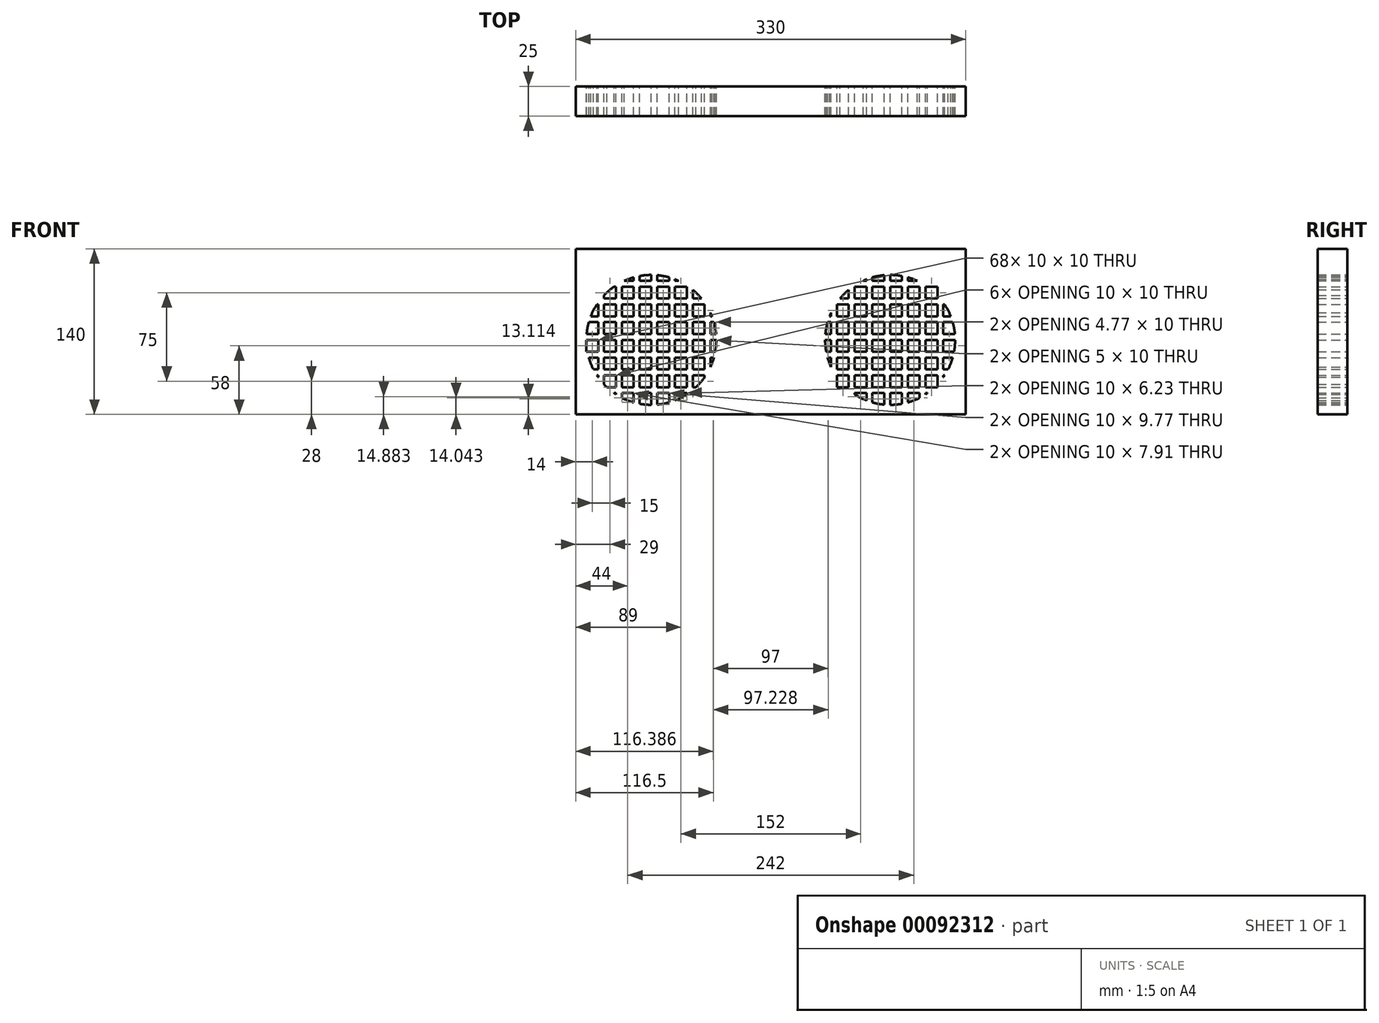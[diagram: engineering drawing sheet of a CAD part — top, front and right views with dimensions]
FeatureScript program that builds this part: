
annotation { "Feature Type Name" : "Feature", "Feature Type Description" : "" }
export const myFeature = defineFeature(function(context is Context, id is Id, definition is map)
    precondition{}
    {
        {
            var Q0;
            Q0=qCreatedBy(makeId("Front.planeOp"),FACE);
            var sketch = newSketch(context, id + "F0", { "sketchPlane" : qUnion([Q0])});
            skLineSegment(sketch, "E0.bottom", {"start": v(0, 0) * mm, "end": v(-165, 0) * mm});
            skLineSegment(sketch, "E0.top", {"start": v(0, 140) * mm, "end": v(-165, 140) * mm});
            skLineSegment(sketch, "E0.left", {"start": v(0, 0) * mm, "end": v(0, 140) * mm});
            skLineSegment(sketch, "E0.right", {"start": v(-165, 0) * mm, "end": v(-165, 140) * mm});
            skCircle(sketch, "E1", {"center": v(-101, 63) * mm, "radius": 55 * mm});
            skLineSegment(sketch, "E2.bottom", {"start": v(-156, 8) * mm, "end": v(-146, 8) * mm});
            skLineSegment(sketch, "E2.top", {"start": v(-156, 18) * mm, "end": v(-146, 18) * mm});
            skLineSegment(sketch, "E2.left", {"start": v(-156, 8) * mm, "end": v(-156, 18) * mm});
            skLineSegment(sketch, "E2.right", {"start": v(-146, 8) * mm, "end": v(-146, 18) * mm});
            skLineSegment(sketch, "E3.0.1.0", {"start": v(-156, 23) * mm, "end": v(-146, 23) * mm});
            skLineSegment(sketch, "E3.0.1.1", {"start": v(-156, 33) * mm, "end": v(-146, 33) * mm});
            skLineSegment(sketch, "E3.0.1.2", {"start": v(-156, 23) * mm, "end": v(-156, 33) * mm});
            skLineSegment(sketch, "E3.0.1.3", {"start": v(-146, 23) * mm, "end": v(-146, 33) * mm});
            skLineSegment(sketch, "E3.0.2.0", {"start": v(-156, 38) * mm, "end": v(-146, 38) * mm});
            skLineSegment(sketch, "E3.0.2.1", {"start": v(-156, 48) * mm, "end": v(-146, 48) * mm});
            skLineSegment(sketch, "E3.0.2.2", {"start": v(-156, 38) * mm, "end": v(-156, 48) * mm});
            skLineSegment(sketch, "E3.0.2.3", {"start": v(-146, 38) * mm, "end": v(-146, 48) * mm});
            skLineSegment(sketch, "E3.0.3.0", {"start": v(-156, 53) * mm, "end": v(-146, 53) * mm});
            skLineSegment(sketch, "E3.0.3.1", {"start": v(-156, 63) * mm, "end": v(-146, 63) * mm});
            skLineSegment(sketch, "E3.0.3.2", {"start": v(-156, 53) * mm, "end": v(-156, 63) * mm});
            skLineSegment(sketch, "E3.0.3.3", {"start": v(-146, 53) * mm, "end": v(-146, 63) * mm});
            skLineSegment(sketch, "E3.0.4.0", {"start": v(-156, 68) * mm, "end": v(-146, 68) * mm});
            skLineSegment(sketch, "E3.0.4.1", {"start": v(-156, 78) * mm, "end": v(-146, 78) * mm});
            skLineSegment(sketch, "E3.0.4.2", {"start": v(-156, 68) * mm, "end": v(-156, 78) * mm});
            skLineSegment(sketch, "E3.0.4.3", {"start": v(-146, 68) * mm, "end": v(-146, 78) * mm});
            skLineSegment(sketch, "E3.0.5.0", {"start": v(-156, 83) * mm, "end": v(-146, 83) * mm});
            skLineSegment(sketch, "E3.0.5.1", {"start": v(-156, 93) * mm, "end": v(-146, 93) * mm});
            skLineSegment(sketch, "E3.0.5.2", {"start": v(-156, 83) * mm, "end": v(-156, 93) * mm});
            skLineSegment(sketch, "E3.0.5.3", {"start": v(-146, 83) * mm, "end": v(-146, 93) * mm});
            skLineSegment(sketch, "E3.0.6.0", {"start": v(-156, 98) * mm, "end": v(-146, 98) * mm});
            skLineSegment(sketch, "E3.0.6.1", {"start": v(-156, 108) * mm, "end": v(-146, 108) * mm});
            skLineSegment(sketch, "E3.0.6.2", {"start": v(-156, 98) * mm, "end": v(-156, 108) * mm});
            skLineSegment(sketch, "E3.0.6.3", {"start": v(-146, 98) * mm, "end": v(-146, 108) * mm});
            skLineSegment(sketch, "E3.1.0.0", {"start": v(-141, 8) * mm, "end": v(-131, 8) * mm});
            skLineSegment(sketch, "E3.1.0.1", {"start": v(-141, 18) * mm, "end": v(-131, 18) * mm});
            skLineSegment(sketch, "E3.1.0.2", {"start": v(-141, 8) * mm, "end": v(-141, 18) * mm});
            skLineSegment(sketch, "E3.1.0.3", {"start": v(-131, 8) * mm, "end": v(-131, 18) * mm});
            skLineSegment(sketch, "E3.1.1.0", {"start": v(-141, 23) * mm, "end": v(-131, 23) * mm});
            skLineSegment(sketch, "E3.1.1.1", {"start": v(-141, 33) * mm, "end": v(-131, 33) * mm});
            skLineSegment(sketch, "E3.1.1.2", {"start": v(-141, 23) * mm, "end": v(-141, 33) * mm});
            skLineSegment(sketch, "E3.1.1.3", {"start": v(-131, 23) * mm, "end": v(-131, 33) * mm});
            skLineSegment(sketch, "E3.1.2.0", {"start": v(-141, 38) * mm, "end": v(-131, 38) * mm});
            skLineSegment(sketch, "E3.1.2.1", {"start": v(-141, 48) * mm, "end": v(-131, 48) * mm});
            skLineSegment(sketch, "E3.1.2.2", {"start": v(-141, 38) * mm, "end": v(-141, 48) * mm});
            skLineSegment(sketch, "E3.1.2.3", {"start": v(-131, 38) * mm, "end": v(-131, 48) * mm});
            skLineSegment(sketch, "E3.1.3.0", {"start": v(-141, 53) * mm, "end": v(-131, 53) * mm});
            skLineSegment(sketch, "E3.1.3.1", {"start": v(-141, 63) * mm, "end": v(-131, 63) * mm});
            skLineSegment(sketch, "E3.1.3.2", {"start": v(-141, 53) * mm, "end": v(-141, 63) * mm});
            skLineSegment(sketch, "E3.1.3.3", {"start": v(-131, 53) * mm, "end": v(-131, 63) * mm});
            skLineSegment(sketch, "E3.1.4.0", {"start": v(-141, 68) * mm, "end": v(-131, 68) * mm});
            skLineSegment(sketch, "E3.1.4.1", {"start": v(-141, 78) * mm, "end": v(-131, 78) * mm});
            skLineSegment(sketch, "E3.1.4.2", {"start": v(-141, 68) * mm, "end": v(-141, 78) * mm});
            skLineSegment(sketch, "E3.1.4.3", {"start": v(-131, 68) * mm, "end": v(-131, 78) * mm});
            skLineSegment(sketch, "E3.1.5.0", {"start": v(-141, 83) * mm, "end": v(-131, 83) * mm});
            skLineSegment(sketch, "E3.1.5.1", {"start": v(-141, 93) * mm, "end": v(-131, 93) * mm});
            skLineSegment(sketch, "E3.1.5.2", {"start": v(-141, 83) * mm, "end": v(-141, 93) * mm});
            skLineSegment(sketch, "E3.1.5.3", {"start": v(-131, 83) * mm, "end": v(-131, 93) * mm});
            skLineSegment(sketch, "E3.1.6.0", {"start": v(-141, 98) * mm, "end": v(-131, 98) * mm});
            skLineSegment(sketch, "E3.1.6.1", {"start": v(-141, 108) * mm, "end": v(-131, 108) * mm});
            skLineSegment(sketch, "E3.1.6.2", {"start": v(-141, 98) * mm, "end": v(-141, 108) * mm});
            skLineSegment(sketch, "E3.1.6.3", {"start": v(-131, 98) * mm, "end": v(-131, 108) * mm});
            skLineSegment(sketch, "E3.2.0.0", {"start": v(-126, 8) * mm, "end": v(-116, 8) * mm});
            skLineSegment(sketch, "E3.2.0.1", {"start": v(-126, 18) * mm, "end": v(-116, 18) * mm});
            skLineSegment(sketch, "E3.2.0.2", {"start": v(-126, 8) * mm, "end": v(-126, 18) * mm});
            skLineSegment(sketch, "E3.2.0.3", {"start": v(-116, 8) * mm, "end": v(-116, 18) * mm});
            skLineSegment(sketch, "E3.2.1.0", {"start": v(-126, 23) * mm, "end": v(-116, 23) * mm});
            skLineSegment(sketch, "E3.2.1.1", {"start": v(-126, 33) * mm, "end": v(-116, 33) * mm});
            skLineSegment(sketch, "E3.2.1.2", {"start": v(-126, 23) * mm, "end": v(-126, 33) * mm});
            skLineSegment(sketch, "E3.2.1.3", {"start": v(-116, 23) * mm, "end": v(-116, 33) * mm});
            skLineSegment(sketch, "E3.2.2.0", {"start": v(-126, 38) * mm, "end": v(-116, 38) * mm});
            skLineSegment(sketch, "E3.2.2.1", {"start": v(-126, 48) * mm, "end": v(-116, 48) * mm});
            skLineSegment(sketch, "E3.2.2.2", {"start": v(-126, 38) * mm, "end": v(-126, 48) * mm});
            skLineSegment(sketch, "E3.2.2.3", {"start": v(-116, 38) * mm, "end": v(-116, 48) * mm});
            skLineSegment(sketch, "E3.2.3.0", {"start": v(-126, 53) * mm, "end": v(-116, 53) * mm});
            skLineSegment(sketch, "E3.2.3.1", {"start": v(-126, 63) * mm, "end": v(-116, 63) * mm});
            skLineSegment(sketch, "E3.2.3.2", {"start": v(-126, 53) * mm, "end": v(-126, 63) * mm});
            skLineSegment(sketch, "E3.2.3.3", {"start": v(-116, 53) * mm, "end": v(-116, 63) * mm});
            skLineSegment(sketch, "E3.2.4.0", {"start": v(-126, 68) * mm, "end": v(-116, 68) * mm});
            skLineSegment(sketch, "E3.2.4.1", {"start": v(-126, 78) * mm, "end": v(-116, 78) * mm});
            skLineSegment(sketch, "E3.2.4.2", {"start": v(-126, 68) * mm, "end": v(-126, 78) * mm});
            skLineSegment(sketch, "E3.2.4.3", {"start": v(-116, 68) * mm, "end": v(-116, 78) * mm});
            skLineSegment(sketch, "E3.2.5.0", {"start": v(-126, 83) * mm, "end": v(-116, 83) * mm});
            skLineSegment(sketch, "E3.2.5.1", {"start": v(-126, 93) * mm, "end": v(-116, 93) * mm});
            skLineSegment(sketch, "E3.2.5.2", {"start": v(-126, 83) * mm, "end": v(-126, 93) * mm});
            skLineSegment(sketch, "E3.2.5.3", {"start": v(-116, 83) * mm, "end": v(-116, 93) * mm});
            skLineSegment(sketch, "E3.2.6.0", {"start": v(-126, 98) * mm, "end": v(-116, 98) * mm});
            skLineSegment(sketch, "E3.2.6.1", {"start": v(-126, 108) * mm, "end": v(-116, 108) * mm});
            skLineSegment(sketch, "E3.2.6.2", {"start": v(-126, 98) * mm, "end": v(-126, 108) * mm});
            skLineSegment(sketch, "E3.2.6.3", {"start": v(-116, 98) * mm, "end": v(-116, 108) * mm});
            skLineSegment(sketch, "E3.3.0.0", {"start": v(-111, 8) * mm, "end": v(-101, 8) * mm});
            skLineSegment(sketch, "E3.3.0.1", {"start": v(-111, 18) * mm, "end": v(-101, 18) * mm});
            skLineSegment(sketch, "E3.3.0.2", {"start": v(-111, 8) * mm, "end": v(-111, 18) * mm});
            skLineSegment(sketch, "E3.3.0.3", {"start": v(-101, 8) * mm, "end": v(-101, 18) * mm});
            skLineSegment(sketch, "E3.3.1.0", {"start": v(-111, 23) * mm, "end": v(-101, 23) * mm});
            skLineSegment(sketch, "E3.3.1.1", {"start": v(-111, 33) * mm, "end": v(-101, 33) * mm});
            skLineSegment(sketch, "E3.3.1.2", {"start": v(-111, 23) * mm, "end": v(-111, 33) * mm});
            skLineSegment(sketch, "E3.3.1.3", {"start": v(-101, 23) * mm, "end": v(-101, 33) * mm});
            skLineSegment(sketch, "E3.3.2.0", {"start": v(-111, 38) * mm, "end": v(-101, 38) * mm});
            skLineSegment(sketch, "E3.3.2.1", {"start": v(-111, 48) * mm, "end": v(-101, 48) * mm});
            skLineSegment(sketch, "E3.3.2.2", {"start": v(-111, 38) * mm, "end": v(-111, 48) * mm});
            skLineSegment(sketch, "E3.3.2.3", {"start": v(-101, 38) * mm, "end": v(-101, 48) * mm});
            skLineSegment(sketch, "E3.3.3.0", {"start": v(-111, 53) * mm, "end": v(-101, 53) * mm});
            skLineSegment(sketch, "E3.3.3.1", {"start": v(-111, 63) * mm, "end": v(-101, 63) * mm});
            skLineSegment(sketch, "E3.3.3.2", {"start": v(-111, 53) * mm, "end": v(-111, 63) * mm});
            skLineSegment(sketch, "E3.3.3.3", {"start": v(-101, 53) * mm, "end": v(-101, 63) * mm});
            skLineSegment(sketch, "E3.3.4.0", {"start": v(-111, 68) * mm, "end": v(-101, 68) * mm});
            skLineSegment(sketch, "E3.3.4.1", {"start": v(-111, 78) * mm, "end": v(-101, 78) * mm});
            skLineSegment(sketch, "E3.3.4.2", {"start": v(-111, 68) * mm, "end": v(-111, 78) * mm});
            skLineSegment(sketch, "E3.3.4.3", {"start": v(-101, 68) * mm, "end": v(-101, 78) * mm});
            skLineSegment(sketch, "E3.3.5.0", {"start": v(-111, 83) * mm, "end": v(-101, 83) * mm});
            skLineSegment(sketch, "E3.3.5.1", {"start": v(-111, 93) * mm, "end": v(-101, 93) * mm});
            skLineSegment(sketch, "E3.3.5.2", {"start": v(-111, 83) * mm, "end": v(-111, 93) * mm});
            skLineSegment(sketch, "E3.3.5.3", {"start": v(-101, 83) * mm, "end": v(-101, 93) * mm});
            skLineSegment(sketch, "E3.3.6.0", {"start": v(-111, 98) * mm, "end": v(-101, 98) * mm});
            skLineSegment(sketch, "E3.3.6.1", {"start": v(-111, 108) * mm, "end": v(-101, 108) * mm});
            skLineSegment(sketch, "E3.3.6.2", {"start": v(-111, 98) * mm, "end": v(-111, 108) * mm});
            skLineSegment(sketch, "E3.3.6.3", {"start": v(-101, 98) * mm, "end": v(-101, 108) * mm});
            skLineSegment(sketch, "E3.4.0.0", {"start": v(-96, 8) * mm, "end": v(-86, 8) * mm});
            skLineSegment(sketch, "E3.4.0.1", {"start": v(-96, 18) * mm, "end": v(-86, 18) * mm});
            skLineSegment(sketch, "E3.4.0.2", {"start": v(-96, 8) * mm, "end": v(-96, 18) * mm});
            skLineSegment(sketch, "E3.4.0.3", {"start": v(-86, 8) * mm, "end": v(-86, 18) * mm});
            skLineSegment(sketch, "E3.4.1.0", {"start": v(-96, 23) * mm, "end": v(-86, 23) * mm});
            skLineSegment(sketch, "E3.4.1.1", {"start": v(-96, 33) * mm, "end": v(-86, 33) * mm});
            skLineSegment(sketch, "E3.4.1.2", {"start": v(-96, 23) * mm, "end": v(-96, 33) * mm});
            skLineSegment(sketch, "E3.4.1.3", {"start": v(-86, 23) * mm, "end": v(-86, 33) * mm});
            skLineSegment(sketch, "E3.4.2.0", {"start": v(-96, 38) * mm, "end": v(-86, 38) * mm});
            skLineSegment(sketch, "E3.4.2.1", {"start": v(-96, 48) * mm, "end": v(-86, 48) * mm});
            skLineSegment(sketch, "E3.4.2.2", {"start": v(-96, 38) * mm, "end": v(-96, 48) * mm});
            skLineSegment(sketch, "E3.4.2.3", {"start": v(-86, 38) * mm, "end": v(-86, 48) * mm});
            skLineSegment(sketch, "E3.4.3.0", {"start": v(-96, 53) * mm, "end": v(-86, 53) * mm});
            skLineSegment(sketch, "E3.4.3.1", {"start": v(-96, 63) * mm, "end": v(-86, 63) * mm});
            skLineSegment(sketch, "E3.4.3.2", {"start": v(-96, 53) * mm, "end": v(-96, 63) * mm});
            skLineSegment(sketch, "E3.4.3.3", {"start": v(-86, 53) * mm, "end": v(-86, 63) * mm});
            skLineSegment(sketch, "E3.4.4.0", {"start": v(-96, 68) * mm, "end": v(-86, 68) * mm});
            skLineSegment(sketch, "E3.4.4.1", {"start": v(-96, 78) * mm, "end": v(-86, 78) * mm});
            skLineSegment(sketch, "E3.4.4.2", {"start": v(-96, 68) * mm, "end": v(-96, 78) * mm});
            skLineSegment(sketch, "E3.4.4.3", {"start": v(-86, 68) * mm, "end": v(-86, 78) * mm});
            skLineSegment(sketch, "E3.4.5.0", {"start": v(-96, 83) * mm, "end": v(-86, 83) * mm});
            skLineSegment(sketch, "E3.4.5.1", {"start": v(-96, 93) * mm, "end": v(-86, 93) * mm});
            skLineSegment(sketch, "E3.4.5.2", {"start": v(-96, 83) * mm, "end": v(-96, 93) * mm});
            skLineSegment(sketch, "E3.4.5.3", {"start": v(-86, 83) * mm, "end": v(-86, 93) * mm});
            skLineSegment(sketch, "E3.4.6.0", {"start": v(-96, 98) * mm, "end": v(-86, 98) * mm});
            skLineSegment(sketch, "E3.4.6.1", {"start": v(-96, 108) * mm, "end": v(-86, 108) * mm});
            skLineSegment(sketch, "E3.4.6.2", {"start": v(-96, 98) * mm, "end": v(-96, 108) * mm});
            skLineSegment(sketch, "E3.4.6.3", {"start": v(-86, 98) * mm, "end": v(-86, 108) * mm});
            skLineSegment(sketch, "E3.5.0.0", {"start": v(-81, 8) * mm, "end": v(-71, 8) * mm});
            skLineSegment(sketch, "E3.5.0.1", {"start": v(-81, 18) * mm, "end": v(-71, 18) * mm});
            skLineSegment(sketch, "E3.5.0.2", {"start": v(-81, 8) * mm, "end": v(-81, 18) * mm});
            skLineSegment(sketch, "E3.5.0.3", {"start": v(-71, 8) * mm, "end": v(-71, 18) * mm});
            skLineSegment(sketch, "E3.5.1.0", {"start": v(-81, 23) * mm, "end": v(-71, 23) * mm});
            skLineSegment(sketch, "E3.5.1.1", {"start": v(-81, 33) * mm, "end": v(-71, 33) * mm});
            skLineSegment(sketch, "E3.5.1.2", {"start": v(-81, 23) * mm, "end": v(-81, 33) * mm});
            skLineSegment(sketch, "E3.5.1.3", {"start": v(-71, 23) * mm, "end": v(-71, 33) * mm});
            skLineSegment(sketch, "E3.5.2.0", {"start": v(-81, 38) * mm, "end": v(-71, 38) * mm});
            skLineSegment(sketch, "E3.5.2.1", {"start": v(-81, 48) * mm, "end": v(-71, 48) * mm});
            skLineSegment(sketch, "E3.5.2.2", {"start": v(-81, 38) * mm, "end": v(-81, 48) * mm});
            skLineSegment(sketch, "E3.5.2.3", {"start": v(-71, 38) * mm, "end": v(-71, 48) * mm});
            skLineSegment(sketch, "E3.5.3.0", {"start": v(-81, 53) * mm, "end": v(-71, 53) * mm});
            skLineSegment(sketch, "E3.5.3.1", {"start": v(-81, 63) * mm, "end": v(-71, 63) * mm});
            skLineSegment(sketch, "E3.5.3.2", {"start": v(-81, 53) * mm, "end": v(-81, 63) * mm});
            skLineSegment(sketch, "E3.5.3.3", {"start": v(-71, 53) * mm, "end": v(-71, 63) * mm});
            skLineSegment(sketch, "E3.5.4.0", {"start": v(-81, 68) * mm, "end": v(-71, 68) * mm});
            skLineSegment(sketch, "E3.5.4.1", {"start": v(-81, 78) * mm, "end": v(-71, 78) * mm});
            skLineSegment(sketch, "E3.5.4.2", {"start": v(-81, 68) * mm, "end": v(-81, 78) * mm});
            skLineSegment(sketch, "E3.5.4.3", {"start": v(-71, 68) * mm, "end": v(-71, 78) * mm});
            skLineSegment(sketch, "E3.5.5.0", {"start": v(-81, 83) * mm, "end": v(-71, 83) * mm});
            skLineSegment(sketch, "E3.5.5.1", {"start": v(-81, 93) * mm, "end": v(-71, 93) * mm});
            skLineSegment(sketch, "E3.5.5.2", {"start": v(-81, 83) * mm, "end": v(-81, 93) * mm});
            skLineSegment(sketch, "E3.5.5.3", {"start": v(-71, 83) * mm, "end": v(-71, 93) * mm});
            skLineSegment(sketch, "E3.5.6.0", {"start": v(-81, 98) * mm, "end": v(-71, 98) * mm});
            skLineSegment(sketch, "E3.5.6.1", {"start": v(-81, 108) * mm, "end": v(-71, 108) * mm});
            skLineSegment(sketch, "E3.5.6.2", {"start": v(-81, 98) * mm, "end": v(-81, 108) * mm});
            skLineSegment(sketch, "E3.5.6.3", {"start": v(-71, 98) * mm, "end": v(-71, 108) * mm});
            skLineSegment(sketch, "E3.6.0.0", {"start": v(-66, 8) * mm, "end": v(-56, 8) * mm});
            skLineSegment(sketch, "E3.6.0.1", {"start": v(-66, 18) * mm, "end": v(-56, 18) * mm});
            skLineSegment(sketch, "E3.6.0.2", {"start": v(-66, 8) * mm, "end": v(-66, 18) * mm});
            skLineSegment(sketch, "E3.6.0.3", {"start": v(-56, 8) * mm, "end": v(-56, 18) * mm});
            skLineSegment(sketch, "E3.6.1.0", {"start": v(-66, 23) * mm, "end": v(-56, 23) * mm});
            skLineSegment(sketch, "E3.6.1.1", {"start": v(-66, 33) * mm, "end": v(-56, 33) * mm});
            skLineSegment(sketch, "E3.6.1.2", {"start": v(-66, 23) * mm, "end": v(-66, 33) * mm});
            skLineSegment(sketch, "E3.6.1.3", {"start": v(-56, 23) * mm, "end": v(-56, 33) * mm});
            skLineSegment(sketch, "E3.6.2.0", {"start": v(-66, 38) * mm, "end": v(-56, 38) * mm});
            skLineSegment(sketch, "E3.6.2.1", {"start": v(-66, 48) * mm, "end": v(-56, 48) * mm});
            skLineSegment(sketch, "E3.6.2.2", {"start": v(-66, 38) * mm, "end": v(-66, 48) * mm});
            skLineSegment(sketch, "E3.6.2.3", {"start": v(-56, 38) * mm, "end": v(-56, 48) * mm});
            skLineSegment(sketch, "E3.6.3.0", {"start": v(-66, 53) * mm, "end": v(-56, 53) * mm});
            skLineSegment(sketch, "E3.6.3.1", {"start": v(-66, 63) * mm, "end": v(-56, 63) * mm});
            skLineSegment(sketch, "E3.6.3.2", {"start": v(-66, 53) * mm, "end": v(-66, 63) * mm});
            skLineSegment(sketch, "E3.6.3.3", {"start": v(-56, 53) * mm, "end": v(-56, 63) * mm});
            skLineSegment(sketch, "E3.6.4.0", {"start": v(-66, 68) * mm, "end": v(-56, 68) * mm});
            skLineSegment(sketch, "E3.6.4.1", {"start": v(-66, 78) * mm, "end": v(-56, 78) * mm});
            skLineSegment(sketch, "E3.6.4.2", {"start": v(-66, 68) * mm, "end": v(-66, 78) * mm});
            skLineSegment(sketch, "E3.6.4.3", {"start": v(-56, 68) * mm, "end": v(-56, 78) * mm});
            skLineSegment(sketch, "E3.6.5.0", {"start": v(-66, 83) * mm, "end": v(-56, 83) * mm});
            skLineSegment(sketch, "E3.6.5.1", {"start": v(-66, 93) * mm, "end": v(-56, 93) * mm});
            skLineSegment(sketch, "E3.6.5.2", {"start": v(-66, 83) * mm, "end": v(-66, 93) * mm});
            skLineSegment(sketch, "E3.6.5.3", {"start": v(-56, 83) * mm, "end": v(-56, 93) * mm});
            skLineSegment(sketch, "E3.6.6.0", {"start": v(-66, 98) * mm, "end": v(-56, 98) * mm});
            skLineSegment(sketch, "E3.6.6.1", {"start": v(-66, 108) * mm, "end": v(-56, 108) * mm});
            skLineSegment(sketch, "E3.6.6.2", {"start": v(-66, 98) * mm, "end": v(-66, 108) * mm});
            skLineSegment(sketch, "E3.6.6.3", {"start": v(-56, 98) * mm, "end": v(-56, 108) * mm});
            skLineSegment(sketch, "E3.7.0.0", {"start": v(-51, 8) * mm, "end": v(-41, 8) * mm});
            skLineSegment(sketch, "E3.7.0.1", {"start": v(-51, 18) * mm, "end": v(-41, 18) * mm});
            skLineSegment(sketch, "E3.7.0.2", {"start": v(-51, 8) * mm, "end": v(-51, 18) * mm});
            skLineSegment(sketch, "E3.7.0.3", {"start": v(-41, 8) * mm, "end": v(-41, 18) * mm});
            skLineSegment(sketch, "E3.7.1.0", {"start": v(-51, 23) * mm, "end": v(-41, 23) * mm});
            skLineSegment(sketch, "E3.7.1.1", {"start": v(-51, 33) * mm, "end": v(-41, 33) * mm});
            skLineSegment(sketch, "E3.7.1.2", {"start": v(-51, 23) * mm, "end": v(-51, 33) * mm});
            skLineSegment(sketch, "E3.7.1.3", {"start": v(-41, 23) * mm, "end": v(-41, 33) * mm});
            skLineSegment(sketch, "E3.7.2.0", {"start": v(-51, 38) * mm, "end": v(-41, 38) * mm});
            skLineSegment(sketch, "E3.7.2.1", {"start": v(-51, 48) * mm, "end": v(-41, 48) * mm});
            skLineSegment(sketch, "E3.7.2.2", {"start": v(-51, 38) * mm, "end": v(-51, 48) * mm});
            skLineSegment(sketch, "E3.7.2.3", {"start": v(-41, 38) * mm, "end": v(-41, 48) * mm});
            skLineSegment(sketch, "E3.7.3.0", {"start": v(-51, 53) * mm, "end": v(-41, 53) * mm});
            skLineSegment(sketch, "E3.7.3.1", {"start": v(-51, 63) * mm, "end": v(-41, 63) * mm});
            skLineSegment(sketch, "E3.7.3.2", {"start": v(-51, 53) * mm, "end": v(-51, 63) * mm});
            skLineSegment(sketch, "E3.7.3.3", {"start": v(-41, 53) * mm, "end": v(-41, 63) * mm});
            skLineSegment(sketch, "E3.7.4.0", {"start": v(-51, 68) * mm, "end": v(-41, 68) * mm});
            skLineSegment(sketch, "E3.7.4.1", {"start": v(-51, 78) * mm, "end": v(-41, 78) * mm});
            skLineSegment(sketch, "E3.7.4.2", {"start": v(-51, 68) * mm, "end": v(-51, 78) * mm});
            skLineSegment(sketch, "E3.7.4.3", {"start": v(-41, 68) * mm, "end": v(-41, 78) * mm});
            skLineSegment(sketch, "E3.7.5.0", {"start": v(-51, 83) * mm, "end": v(-41, 83) * mm});
            skLineSegment(sketch, "E3.7.5.1", {"start": v(-51, 93) * mm, "end": v(-41, 93) * mm});
            skLineSegment(sketch, "E3.7.5.2", {"start": v(-51, 83) * mm, "end": v(-51, 93) * mm});
            skLineSegment(sketch, "E3.7.5.3", {"start": v(-41, 83) * mm, "end": v(-41, 93) * mm});
            skLineSegment(sketch, "E3.7.6.0", {"start": v(-51, 98) * mm, "end": v(-41, 98) * mm});
            skLineSegment(sketch, "E3.7.6.1", {"start": v(-51, 108) * mm, "end": v(-41, 108) * mm});
            skLineSegment(sketch, "E3.7.6.2", {"start": v(-51, 98) * mm, "end": v(-51, 108) * mm});
            skLineSegment(sketch, "E3.7.6.3", {"start": v(-41, 98) * mm, "end": v(-41, 108) * mm});
            skLineSegment(sketch, "E3.direction1", {"start": v(-156, 8) * mm, "end": v(-141, 8) * mm, "construction": true});
            skLineSegment(sketch, "E3.direction2", {"start": v(-156, 8) * mm, "end": v(-156, 23) * mm, "construction": true});
            skLineSegment(sketch, "E4.0.0.7", {"start": v(-156, 113) * mm, "end": v(-146, 113) * mm});
            skLineSegment(sketch, "E4.3.0.7", {"start": v(-156, 123) * mm, "end": v(-146, 123) * mm});
            skLineSegment(sketch, "E4.6.0.7", {"start": v(-156, 113) * mm, "end": v(-156, 123) * mm});
            skLineSegment(sketch, "E4.9.0.7", {"start": v(-146, 113) * mm, "end": v(-146, 123) * mm});
            skLineSegment(sketch, "E4.0.1.7", {"start": v(-141, 113) * mm, "end": v(-131, 113) * mm});
            skLineSegment(sketch, "E4.3.1.7", {"start": v(-141, 123) * mm, "end": v(-131, 123) * mm});
            skLineSegment(sketch, "E4.6.1.7", {"start": v(-141, 113) * mm, "end": v(-141, 123) * mm});
            skLineSegment(sketch, "E4.9.1.7", {"start": v(-131, 113) * mm, "end": v(-131, 123) * mm});
            skLineSegment(sketch, "E4.0.2.7", {"start": v(-126, 113) * mm, "end": v(-116, 113) * mm});
            skLineSegment(sketch, "E4.3.2.7", {"start": v(-126, 123) * mm, "end": v(-116, 123) * mm});
            skLineSegment(sketch, "E4.6.2.7", {"start": v(-126, 113) * mm, "end": v(-126, 123) * mm});
            skLineSegment(sketch, "E4.9.2.7", {"start": v(-116, 113) * mm, "end": v(-116, 123) * mm});
            skLineSegment(sketch, "E4.0.3.7", {"start": v(-111, 113) * mm, "end": v(-101, 113) * mm});
            skLineSegment(sketch, "E4.3.3.7", {"start": v(-111, 123) * mm, "end": v(-101, 123) * mm});
            skLineSegment(sketch, "E4.6.3.7", {"start": v(-111, 113) * mm, "end": v(-111, 123) * mm});
            skLineSegment(sketch, "E4.9.3.7", {"start": v(-101, 113) * mm, "end": v(-101, 123) * mm});
            skLineSegment(sketch, "E4.0.4.7", {"start": v(-96, 113) * mm, "end": v(-86, 113) * mm});
            skLineSegment(sketch, "E4.3.4.7", {"start": v(-96, 123) * mm, "end": v(-86, 123) * mm});
            skLineSegment(sketch, "E4.6.4.7", {"start": v(-96, 113) * mm, "end": v(-96, 123) * mm});
            skLineSegment(sketch, "E4.9.4.7", {"start": v(-86, 113) * mm, "end": v(-86, 123) * mm});
            skLineSegment(sketch, "E4.0.5.7", {"start": v(-81, 113) * mm, "end": v(-71, 113) * mm});
            skLineSegment(sketch, "E4.3.5.7", {"start": v(-81, 123) * mm, "end": v(-71, 123) * mm});
            skLineSegment(sketch, "E4.6.5.7", {"start": v(-81, 113) * mm, "end": v(-81, 123) * mm});
            skLineSegment(sketch, "E4.9.5.7", {"start": v(-71, 113) * mm, "end": v(-71, 123) * mm});
            skLineSegment(sketch, "E4.0.6.7", {"start": v(-66, 113) * mm, "end": v(-56, 113) * mm});
            skLineSegment(sketch, "E4.3.6.7", {"start": v(-66, 123) * mm, "end": v(-56, 123) * mm});
            skLineSegment(sketch, "E4.6.6.7", {"start": v(-66, 113) * mm, "end": v(-66, 123) * mm});
            skLineSegment(sketch, "E4.9.6.7", {"start": v(-56, 113) * mm, "end": v(-56, 123) * mm});
            skLineSegment(sketch, "E4.0.7.7", {"start": v(-51, 113) * mm, "end": v(-41, 113) * mm});
            skLineSegment(sketch, "E4.3.7.7", {"start": v(-51, 123) * mm, "end": v(-41, 123) * mm});
            skLineSegment(sketch, "E4.6.7.7", {"start": v(-51, 113) * mm, "end": v(-51, 123) * mm});
            skLineSegment(sketch, "E4.9.7.7", {"start": v(-41, 113) * mm, "end": v(-41, 123) * mm});
            skLineSegment(sketch, "E5.MirrorCS", {"start": v(146, 23) * mm, "end": v(146, 33) * mm});
            skLineSegment(sketch, "E6.MirrorCS", {"start": v(156, 23) * mm, "end": v(156, 33) * mm});
            skLineSegment(sketch, "E7.MirrorCS", {"start": v(156, 23) * mm, "end": v(146, 23) * mm});
            skLineSegment(sketch, "E8.MirrorCS", {"start": v(156, 38) * mm, "end": v(146, 38) * mm});
            skLineSegment(sketch, "E9.MirrorCS", {"start": v(156, 53) * mm, "end": v(156, 63) * mm});
            skLineSegment(sketch, "E10.MirrorCS", {"start": v(96, 8) * mm, "end": v(86, 8) * mm});
            skLineSegment(sketch, "E11.MirrorCS", {"start": v(51, 53) * mm, "end": v(41, 53) * mm});
            skLineSegment(sketch, "E12.MirrorCS", {"start": v(156, 8) * mm, "end": v(156, 23) * mm, "construction": true});
            skLineSegment(sketch, "E13.MirrorCS", {"start": v(156, 8) * mm, "end": v(141, 8) * mm, "construction": true});
            skLineSegment(sketch, "E14.MirrorCS", {"start": v(51, 63) * mm, "end": v(41, 63) * mm});
            skLineSegment(sketch, "E15.MirrorCS", {"start": v(101, 113) * mm, "end": v(101, 123) * mm});
            skLineSegment(sketch, "E16.MirrorCS", {"start": v(156, 83) * mm, "end": v(146, 83) * mm});
            skLineSegment(sketch, "E17.MirrorCS", {"start": v(111, 8) * mm, "end": v(101, 8) * mm});
            skLineSegment(sketch, "E18.MirrorCS", {"start": v(96, 113) * mm, "end": v(96, 123) * mm});
            skLineSegment(sketch, "E19.MirrorCS", {"start": v(51, 68) * mm, "end": v(41, 68) * mm});
            skLineSegment(sketch, "E20.MirrorCS", {"start": v(156, 33) * mm, "end": v(146, 33) * mm});
            skLineSegment(sketch, "E21.MirrorCS", {"start": v(146, 8) * mm, "end": v(146, 18) * mm});
            skLineSegment(sketch, "E22.MirrorCS", {"start": v(156, 8) * mm, "end": v(156, 18) * mm});
            skLineSegment(sketch, "E23.MirrorCS", {"start": v(156, 18) * mm, "end": v(146, 18) * mm});
            skLineSegment(sketch, "E24.MirrorCS", {"start": v(156, 8) * mm, "end": v(146, 8) * mm});
            skCircle(sketch, "E25.MirrorC", {"center": v(101, 63) * mm, "radius": 55 * mm});
            skLineSegment(sketch, "E26.MirrorCS", {"start": v(165, 0) * mm, "end": v(165, 140) * mm});
            skLineSegment(sketch, "E27.MirrorCS", {"start": v(0, 140) * mm, "end": v(165, 140) * mm});
            skLineSegment(sketch, "E28.MirrorCS", {"start": v(0, 0) * mm, "end": v(165, 0) * mm});
            skLineSegment(sketch, "E29.MirrorCS", {"start": v(156, 38) * mm, "end": v(156, 48) * mm});
            skLineSegment(sketch, "E30.MirrorCS", {"start": v(156, 48) * mm, "end": v(146, 48) * mm});
            skLineSegment(sketch, "E31.MirrorCS", {"start": v(41, 8) * mm, "end": v(41, 18) * mm});
            skLineSegment(sketch, "E32.MirrorCS", {"start": v(41, 68) * mm, "end": v(41, 78) * mm});
            skLineSegment(sketch, "E33.MirrorCS", {"start": v(141, 123) * mm, "end": v(131, 123) * mm});
            skLineSegment(sketch, "E34.MirrorCS", {"start": v(81, 123) * mm, "end": v(71, 123) * mm});
            skLineSegment(sketch, "E35.MirrorCS", {"start": v(86, 83) * mm, "end": v(86, 93) * mm});
            skLineSegment(sketch, "E36.MirrorCS", {"start": v(71, 38) * mm, "end": v(71, 48) * mm});
            skLineSegment(sketch, "E37.MirrorCS", {"start": v(71, 98) * mm, "end": v(71, 108) * mm});
            skLineSegment(sketch, "E38.MirrorCS", {"start": v(56, 53) * mm, "end": v(56, 63) * mm});
            skLineSegment(sketch, "E39.MirrorCS", {"start": v(116, 53) * mm, "end": v(116, 63) * mm});
            skLineSegment(sketch, "E40.MirrorCS", {"start": v(101, 8) * mm, "end": v(101, 18) * mm});
            skLineSegment(sketch, "E41.MirrorCS", {"start": v(101, 68) * mm, "end": v(101, 78) * mm});
            skLineSegment(sketch, "E42.MirrorCS", {"start": v(86, 23) * mm, "end": v(86, 33) * mm});
            skLineSegment(sketch, "E43.MirrorCS", {"start": v(146, 83) * mm, "end": v(146, 93) * mm});
            skLineSegment(sketch, "E44.MirrorCS", {"start": v(131, 38) * mm, "end": v(131, 48) * mm});
            skLineSegment(sketch, "E45.MirrorCS", {"start": v(126, 68) * mm, "end": v(116, 68) * mm});
            skLineSegment(sketch, "E46.MirrorCS", {"start": v(126, 8) * mm, "end": v(116, 8) * mm});
            skLineSegment(sketch, "E47.MirrorCS", {"start": v(141, 53) * mm, "end": v(131, 53) * mm});
            skLineSegment(sketch, "E48.MirrorCS", {"start": v(156, 98) * mm, "end": v(146, 98) * mm});
            skLineSegment(sketch, "E49.MirrorCS", {"start": v(96, 98) * mm, "end": v(86, 98) * mm});
            skLineSegment(sketch, "E50.MirrorCS", {"start": v(96, 38) * mm, "end": v(86, 38) * mm});
            skLineSegment(sketch, "E51.MirrorCS", {"start": v(111, 83) * mm, "end": v(101, 83) * mm});
            skLineSegment(sketch, "E52.MirrorCS", {"start": v(111, 23) * mm, "end": v(101, 23) * mm});
            skLineSegment(sketch, "E53.MirrorCS", {"start": v(51, 23) * mm, "end": v(41, 23) * mm});
            skLineSegment(sketch, "E54.MirrorCS", {"start": v(66, 68) * mm, "end": v(56, 68) * mm});
            skLineSegment(sketch, "E55.MirrorCS", {"start": v(66, 8) * mm, "end": v(56, 8) * mm});
            skLineSegment(sketch, "E56.MirrorCS", {"start": v(81, 113) * mm, "end": v(81, 123) * mm});
            skLineSegment(sketch, "E57.MirrorCS", {"start": v(81, 53) * mm, "end": v(71, 53) * mm});
            skLineSegment(sketch, "E58.MirrorCS", {"start": v(141, 113) * mm, "end": v(141, 123) * mm});
            skLineSegment(sketch, "E59.MirrorCS", {"start": v(51, 83) * mm, "end": v(41, 83) * mm});
            skLineSegment(sketch, "E60.MirrorCS", {"start": v(126, 78) * mm, "end": v(116, 78) * mm});
            skLineSegment(sketch, "E61.MirrorCS", {"start": v(126, 18) * mm, "end": v(116, 18) * mm});
            skLineSegment(sketch, "E62.MirrorCS", {"start": v(141, 63) * mm, "end": v(131, 63) * mm});
            skLineSegment(sketch, "E63.MirrorCS", {"start": v(156, 108) * mm, "end": v(146, 108) * mm});
            skLineSegment(sketch, "E64.MirrorCS", {"start": v(96, 108) * mm, "end": v(86, 108) * mm});
            skLineSegment(sketch, "E65.MirrorCS", {"start": v(96, 48) * mm, "end": v(86, 48) * mm});
            skLineSegment(sketch, "E66.MirrorCS", {"start": v(111, 93) * mm, "end": v(101, 93) * mm});
            skLineSegment(sketch, "E67.MirrorCS", {"start": v(111, 33) * mm, "end": v(101, 33) * mm});
            skLineSegment(sketch, "E68.MirrorCS", {"start": v(51, 33) * mm, "end": v(41, 33) * mm});
            skLineSegment(sketch, "E69.MirrorCS", {"start": v(66, 18) * mm, "end": v(56, 18) * mm});
            skLineSegment(sketch, "E70.MirrorCS", {"start": v(66, 78) * mm, "end": v(56, 78) * mm});
            skLineSegment(sketch, "E71.MirrorCS", {"start": v(71, 113) * mm, "end": v(71, 123) * mm});
            skLineSegment(sketch, "E72.MirrorCS", {"start": v(81, 63) * mm, "end": v(71, 63) * mm});
            skLineSegment(sketch, "E73.MirrorCS", {"start": v(51, 93) * mm, "end": v(41, 93) * mm});
            skLineSegment(sketch, "E74.MirrorCS", {"start": v(131, 113) * mm, "end": v(131, 123) * mm});
            skLineSegment(sketch, "E75.MirrorCS", {"start": v(126, 68) * mm, "end": v(126, 78) * mm});
            skLineSegment(sketch, "E76.MirrorCS", {"start": v(126, 8) * mm, "end": v(126, 18) * mm});
            skLineSegment(sketch, "E77.MirrorCS", {"start": v(141, 53) * mm, "end": v(141, 63) * mm});
            skLineSegment(sketch, "E78.MirrorCS", {"start": v(156, 98) * mm, "end": v(156, 108) * mm});
            skLineSegment(sketch, "E79.MirrorCS", {"start": v(96, 98) * mm, "end": v(96, 108) * mm});
            skLineSegment(sketch, "E80.MirrorCS", {"start": v(96, 38) * mm, "end": v(96, 48) * mm});
            skLineSegment(sketch, "E81.MirrorCS", {"start": v(111, 83) * mm, "end": v(111, 93) * mm});
            skLineSegment(sketch, "E82.MirrorCS", {"start": v(111, 23) * mm, "end": v(111, 33) * mm});
            skLineSegment(sketch, "E83.MirrorCS", {"start": v(51, 23) * mm, "end": v(51, 33) * mm});
            skLineSegment(sketch, "E84.MirrorCS", {"start": v(66, 8) * mm, "end": v(66, 18) * mm});
            skLineSegment(sketch, "E85.MirrorCS", {"start": v(66, 68) * mm, "end": v(66, 78) * mm});
            skLineSegment(sketch, "E86.MirrorCS", {"start": v(81, 53) * mm, "end": v(81, 63) * mm});
            skLineSegment(sketch, "E87.MirrorCS", {"start": v(66, 113) * mm, "end": v(56, 113) * mm});
            skLineSegment(sketch, "E88.MirrorCS", {"start": v(126, 113) * mm, "end": v(116, 113) * mm});
            skLineSegment(sketch, "E89.MirrorCS", {"start": v(51, 83) * mm, "end": v(51, 93) * mm});
            skLineSegment(sketch, "E90.MirrorCS", {"start": v(86, 98) * mm, "end": v(86, 108) * mm});
            skLineSegment(sketch, "E91.MirrorCS", {"start": v(86, 38) * mm, "end": v(86, 48) * mm});
            skLineSegment(sketch, "E92.MirrorCS", {"start": v(101, 83) * mm, "end": v(101, 93) * mm});
            skLineSegment(sketch, "E93.MirrorCS", {"start": v(101, 23) * mm, "end": v(101, 33) * mm});
            skLineSegment(sketch, "E94.MirrorCS", {"start": v(41, 23) * mm, "end": v(41, 33) * mm});
            skLineSegment(sketch, "E95.MirrorCS", {"start": v(56, 68) * mm, "end": v(56, 78) * mm});
            skLineSegment(sketch, "E96.MirrorCS", {"start": v(56, 8) * mm, "end": v(56, 18) * mm});
            skLineSegment(sketch, "E97.MirrorCS", {"start": v(71, 53) * mm, "end": v(71, 63) * mm});
            skLineSegment(sketch, "E98.MirrorCS", {"start": v(126, 123) * mm, "end": v(116, 123) * mm});
            skLineSegment(sketch, "E99.MirrorCS", {"start": v(66, 123) * mm, "end": v(56, 123) * mm});
            skLineSegment(sketch, "E100.MirrorCS", {"start": v(41, 83) * mm, "end": v(41, 93) * mm});
            skLineSegment(sketch, "E101.MirrorCS", {"start": v(146, 38) * mm, "end": v(146, 48) * mm});
            skLineSegment(sketch, "E102.MirrorCS", {"start": v(116, 68) * mm, "end": v(116, 78) * mm});
            skLineSegment(sketch, "E103.MirrorCS", {"start": v(116, 8) * mm, "end": v(116, 18) * mm});
            skLineSegment(sketch, "E104.MirrorCS", {"start": v(131, 53) * mm, "end": v(131, 63) * mm});
            skLineSegment(sketch, "E105.MirrorCS", {"start": v(146, 98) * mm, "end": v(146, 108) * mm});
            skLineSegment(sketch, "E106.MirrorCS", {"start": v(51, 38) * mm, "end": v(41, 38) * mm});
            skLineSegment(sketch, "E107.MirrorCS", {"start": v(66, 83) * mm, "end": v(56, 83) * mm});
            skLineSegment(sketch, "E108.MirrorCS", {"start": v(66, 23) * mm, "end": v(56, 23) * mm});
            skLineSegment(sketch, "E109.MirrorCS", {"start": v(81, 68) * mm, "end": v(71, 68) * mm});
            skLineSegment(sketch, "E110.MirrorCS", {"start": v(66, 113) * mm, "end": v(66, 123) * mm});
            skLineSegment(sketch, "E111.MirrorCS", {"start": v(126, 113) * mm, "end": v(126, 123) * mm});
            skLineSegment(sketch, "E112.MirrorCS", {"start": v(51, 98) * mm, "end": v(41, 98) * mm});
            skLineSegment(sketch, "E113.MirrorCS", {"start": v(156, 53) * mm, "end": v(146, 53) * mm});
            skLineSegment(sketch, "E114.MirrorCS", {"start": v(126, 83) * mm, "end": v(116, 83) * mm});
            skLineSegment(sketch, "E115.MirrorCS", {"start": v(126, 23) * mm, "end": v(116, 23) * mm});
            skLineSegment(sketch, "E116.MirrorCS", {"start": v(141, 68) * mm, "end": v(131, 68) * mm});
            skLineSegment(sketch, "E117.MirrorCS", {"start": v(141, 8) * mm, "end": v(131, 8) * mm});
            skLineSegment(sketch, "E118.MirrorCS", {"start": v(81, 8) * mm, "end": v(71, 8) * mm});
            skLineSegment(sketch, "E119.MirrorCS", {"start": v(96, 53) * mm, "end": v(86, 53) * mm});
            skLineSegment(sketch, "E120.MirrorCS", {"start": v(111, 98) * mm, "end": v(101, 98) * mm});
            skLineSegment(sketch, "E121.MirrorCS", {"start": v(111, 38) * mm, "end": v(101, 38) * mm});
            skLineSegment(sketch, "E122.MirrorCS", {"start": v(56, 113) * mm, "end": v(56, 123) * mm});
            skLineSegment(sketch, "E123.MirrorCS", {"start": v(116, 113) * mm, "end": v(116, 123) * mm});
            skLineSegment(sketch, "E124.MirrorCS", {"start": v(51, 108) * mm, "end": v(41, 108) * mm});
            skLineSegment(sketch, "E125.MirrorCS", {"start": v(156, 63) * mm, "end": v(146, 63) * mm});
            skLineSegment(sketch, "E126.MirrorCS", {"start": v(126, 93) * mm, "end": v(116, 93) * mm});
            skLineSegment(sketch, "E127.MirrorCS", {"start": v(126, 33) * mm, "end": v(116, 33) * mm});
            skLineSegment(sketch, "E128.MirrorCS", {"start": v(141, 78) * mm, "end": v(131, 78) * mm});
            skLineSegment(sketch, "E129.MirrorCS", {"start": v(141, 18) * mm, "end": v(131, 18) * mm});
            skLineSegment(sketch, "E130.MirrorCS", {"start": v(81, 18) * mm, "end": v(71, 18) * mm});
            skLineSegment(sketch, "E131.MirrorCS", {"start": v(96, 63) * mm, "end": v(86, 63) * mm});
            skLineSegment(sketch, "E132.MirrorCS", {"start": v(111, 108) * mm, "end": v(101, 108) * mm});
            skLineSegment(sketch, "E133.MirrorCS", {"start": v(111, 48) * mm, "end": v(101, 48) * mm});
            skLineSegment(sketch, "E134.MirrorCS", {"start": v(51, 48) * mm, "end": v(41, 48) * mm});
            skLineSegment(sketch, "E135.MirrorCS", {"start": v(66, 93) * mm, "end": v(56, 93) * mm});
            skLineSegment(sketch, "E136.MirrorCS", {"start": v(66, 33) * mm, "end": v(56, 33) * mm});
            skLineSegment(sketch, "E137.MirrorCS", {"start": v(81, 78) * mm, "end": v(71, 78) * mm});
            skLineSegment(sketch, "E138.MirrorCS", {"start": v(126, 83) * mm, "end": v(126, 93) * mm});
            skLineSegment(sketch, "E139.MirrorCS", {"start": v(126, 23) * mm, "end": v(126, 33) * mm});
            skLineSegment(sketch, "E140.MirrorCS", {"start": v(141, 68) * mm, "end": v(141, 78) * mm});
            skLineSegment(sketch, "E141.MirrorCS", {"start": v(141, 8) * mm, "end": v(141, 18) * mm});
            skLineSegment(sketch, "E142.MirrorCS", {"start": v(81, 8) * mm, "end": v(81, 18) * mm});
            skLineSegment(sketch, "E143.MirrorCS", {"start": v(96, 53) * mm, "end": v(96, 63) * mm});
            skLineSegment(sketch, "E144.MirrorCS", {"start": v(111, 98) * mm, "end": v(111, 108) * mm});
            skLineSegment(sketch, "E145.MirrorCS", {"start": v(111, 38) * mm, "end": v(111, 48) * mm});
            skLineSegment(sketch, "E146.MirrorCS", {"start": v(51, 38) * mm, "end": v(51, 48) * mm});
            skLineSegment(sketch, "E147.MirrorCS", {"start": v(66, 83) * mm, "end": v(66, 93) * mm});
            skLineSegment(sketch, "E148.MirrorCS", {"start": v(66, 23) * mm, "end": v(66, 33) * mm});
            skLineSegment(sketch, "E149.MirrorCS", {"start": v(81, 68) * mm, "end": v(81, 78) * mm});
            skLineSegment(sketch, "E150.MirrorCS", {"start": v(51, 113) * mm, "end": v(41, 113) * mm});
            skLineSegment(sketch, "E151.MirrorCS", {"start": v(51, 98) * mm, "end": v(51, 108) * mm});
            skLineSegment(sketch, "E152.MirrorCS", {"start": v(111, 113) * mm, "end": v(101, 113) * mm});
            skLineSegment(sketch, "E153.MirrorCS", {"start": v(146, 53) * mm, "end": v(146, 63) * mm});
            skLineSegment(sketch, "E154.MirrorCS", {"start": v(116, 83) * mm, "end": v(116, 93) * mm});
            skLineSegment(sketch, "E155.MirrorCS", {"start": v(116, 23) * mm, "end": v(116, 33) * mm});
            skLineSegment(sketch, "E156.MirrorCS", {"start": v(131, 68) * mm, "end": v(131, 78) * mm});
            skLineSegment(sketch, "E157.MirrorCS", {"start": v(131, 8) * mm, "end": v(131, 18) * mm});
            skLineSegment(sketch, "E158.MirrorCS", {"start": v(71, 8) * mm, "end": v(71, 18) * mm});
            skLineSegment(sketch, "E159.MirrorCS", {"start": v(86, 53) * mm, "end": v(86, 63) * mm});
            skLineSegment(sketch, "E160.MirrorCS", {"start": v(101, 98) * mm, "end": v(101, 108) * mm});
            skLineSegment(sketch, "E161.MirrorCS", {"start": v(101, 38) * mm, "end": v(101, 48) * mm});
            skLineSegment(sketch, "E162.MirrorCS", {"start": v(41, 38) * mm, "end": v(41, 48) * mm});
            skLineSegment(sketch, "E163.MirrorCS", {"start": v(56, 83) * mm, "end": v(56, 93) * mm});
            skLineSegment(sketch, "E164.MirrorCS", {"start": v(56, 23) * mm, "end": v(56, 33) * mm});
            skLineSegment(sketch, "E165.MirrorCS", {"start": v(71, 68) * mm, "end": v(71, 78) * mm});
            skLineSegment(sketch, "E166.MirrorCS", {"start": v(111, 123) * mm, "end": v(101, 123) * mm});
            skLineSegment(sketch, "E167.MirrorCS", {"start": v(51, 123) * mm, "end": v(41, 123) * mm});
            skLineSegment(sketch, "E168.MirrorCS", {"start": v(41, 98) * mm, "end": v(41, 108) * mm});
            skLineSegment(sketch, "E169.MirrorCS", {"start": v(156, 68) * mm, "end": v(146, 68) * mm});
            skLineSegment(sketch, "E170.MirrorCS", {"start": v(126, 98) * mm, "end": v(116, 98) * mm});
            skLineSegment(sketch, "E171.MirrorCS", {"start": v(126, 38) * mm, "end": v(116, 38) * mm});
            skLineSegment(sketch, "E172.MirrorCS", {"start": v(141, 83) * mm, "end": v(131, 83) * mm});
            skLineSegment(sketch, "E173.MirrorCS", {"start": v(141, 23) * mm, "end": v(131, 23) * mm});
            skLineSegment(sketch, "E174.MirrorCS", {"start": v(81, 23) * mm, "end": v(71, 23) * mm});
            skLineSegment(sketch, "E175.MirrorCS", {"start": v(96, 68) * mm, "end": v(86, 68) * mm});
            skLineSegment(sketch, "E176.MirrorCS", {"start": v(111, 53) * mm, "end": v(101, 53) * mm});
            skLineSegment(sketch, "E177.MirrorCS", {"start": v(66, 98) * mm, "end": v(56, 98) * mm});
            skLineSegment(sketch, "E178.MirrorCS", {"start": v(66, 38) * mm, "end": v(56, 38) * mm});
            skLineSegment(sketch, "E179.MirrorCS", {"start": v(81, 83) * mm, "end": v(71, 83) * mm});
            skLineSegment(sketch, "E180.MirrorCS", {"start": v(51, 113) * mm, "end": v(51, 123) * mm});
            skLineSegment(sketch, "E181.MirrorCS", {"start": v(111, 113) * mm, "end": v(111, 123) * mm});
            skLineSegment(sketch, "E182.MirrorCS", {"start": v(156, 78) * mm, "end": v(146, 78) * mm});
            skLineSegment(sketch, "E183.MirrorCS", {"start": v(126, 108) * mm, "end": v(116, 108) * mm});
            skLineSegment(sketch, "E184.MirrorCS", {"start": v(126, 48) * mm, "end": v(116, 48) * mm});
            skLineSegment(sketch, "E185.MirrorCS", {"start": v(141, 93) * mm, "end": v(131, 93) * mm});
            skLineSegment(sketch, "E186.MirrorCS", {"start": v(141, 33) * mm, "end": v(131, 33) * mm});
            skLineSegment(sketch, "E187.MirrorCS", {"start": v(81, 33) * mm, "end": v(71, 33) * mm});
            skLineSegment(sketch, "E188.MirrorCS", {"start": v(96, 78) * mm, "end": v(86, 78) * mm});
            skLineSegment(sketch, "E189.MirrorCS", {"start": v(96, 18) * mm, "end": v(86, 18) * mm});
            skLineSegment(sketch, "E190.MirrorCS", {"start": v(111, 63) * mm, "end": v(101, 63) * mm});
            skLineSegment(sketch, "E191.MirrorCS", {"start": v(66, 108) * mm, "end": v(56, 108) * mm});
            skLineSegment(sketch, "E192.MirrorCS", {"start": v(66, 48) * mm, "end": v(56, 48) * mm});
            skLineSegment(sketch, "E193.MirrorCS", {"start": v(81, 93) * mm, "end": v(71, 93) * mm});
            skLineSegment(sketch, "E194.MirrorCS", {"start": v(41, 113) * mm, "end": v(41, 123) * mm});
            skLineSegment(sketch, "E195.MirrorCS", {"start": v(141, 83) * mm, "end": v(141, 93) * mm});
            skLineSegment(sketch, "E196.MirrorCS", {"start": v(141, 23) * mm, "end": v(141, 33) * mm});
            skLineSegment(sketch, "E197.MirrorCS", {"start": v(156, 68) * mm, "end": v(156, 78) * mm});
            skLineSegment(sketch, "E198.MirrorCS", {"start": v(96, 8) * mm, "end": v(96, 18) * mm});
            skLineSegment(sketch, "E199.MirrorCS", {"start": v(111, 53) * mm, "end": v(111, 63) * mm});
            skLineSegment(sketch, "E200.MirrorCS", {"start": v(126, 98) * mm, "end": v(126, 108) * mm});
            skLineSegment(sketch, "E201.MirrorCS", {"start": v(126, 38) * mm, "end": v(126, 48) * mm});
            skLineSegment(sketch, "E202.MirrorCS", {"start": v(66, 38) * mm, "end": v(66, 48) * mm});
            skLineSegment(sketch, "E203.MirrorCS", {"start": v(81, 83) * mm, "end": v(81, 93) * mm});
            skLineSegment(sketch, "E204.MirrorCS", {"start": v(81, 23) * mm, "end": v(81, 33) * mm});
            skLineSegment(sketch, "E205.MirrorCS", {"start": v(96, 68) * mm, "end": v(96, 78) * mm});
            skLineSegment(sketch, "E206.MirrorCS", {"start": v(96, 113) * mm, "end": v(86, 113) * mm});
            skLineSegment(sketch, "E207.MirrorCS", {"start": v(156, 113) * mm, "end": v(146, 113) * mm});
            skLineSegment(sketch, "E208.MirrorCS", {"start": v(51, 53) * mm, "end": v(51, 63) * mm});
            skLineSegment(sketch, "E209.MirrorCS", {"start": v(66, 98) * mm, "end": v(66, 108) * mm});
            skLineSegment(sketch, "E210.MirrorCS", {"start": v(131, 83) * mm, "end": v(131, 93) * mm});
            skLineSegment(sketch, "E211.MirrorCS", {"start": v(131, 23) * mm, "end": v(131, 33) * mm});
            skLineSegment(sketch, "E212.MirrorCS", {"start": v(146, 68) * mm, "end": v(146, 78) * mm});
            skLineSegment(sketch, "E213.MirrorCS", {"start": v(86, 8) * mm, "end": v(86, 18) * mm});
            skLineSegment(sketch, "E214.MirrorCS", {"start": v(101, 53) * mm, "end": v(101, 63) * mm});
            skLineSegment(sketch, "E215.MirrorCS", {"start": v(116, 98) * mm, "end": v(116, 108) * mm});
            skLineSegment(sketch, "E216.MirrorCS", {"start": v(116, 38) * mm, "end": v(116, 48) * mm});
            skLineSegment(sketch, "E217.MirrorCS", {"start": v(56, 38) * mm, "end": v(56, 48) * mm});
            skLineSegment(sketch, "E218.MirrorCS", {"start": v(71, 83) * mm, "end": v(71, 93) * mm});
            skLineSegment(sketch, "E219.MirrorCS", {"start": v(71, 23) * mm, "end": v(71, 33) * mm});
            skLineSegment(sketch, "E220.MirrorCS", {"start": v(86, 68) * mm, "end": v(86, 78) * mm});
            skLineSegment(sketch, "E221.MirrorCS", {"start": v(96, 123) * mm, "end": v(86, 123) * mm});
            skLineSegment(sketch, "E222.MirrorCS", {"start": v(156, 123) * mm, "end": v(146, 123) * mm});
            skLineSegment(sketch, "E223.MirrorCS", {"start": v(41, 53) * mm, "end": v(41, 63) * mm});
            skLineSegment(sketch, "E224.MirrorCS", {"start": v(56, 98) * mm, "end": v(56, 108) * mm});
            skLineSegment(sketch, "E225.MirrorCS", {"start": v(141, 98) * mm, "end": v(131, 98) * mm});
            skLineSegment(sketch, "E226.MirrorCS", {"start": v(141, 38) * mm, "end": v(131, 38) * mm});
            skLineSegment(sketch, "E227.MirrorCS", {"start": v(96, 23) * mm, "end": v(86, 23) * mm});
            skLineSegment(sketch, "E228.MirrorCS", {"start": v(111, 68) * mm, "end": v(101, 68) * mm});
            skLineSegment(sketch, "E229.MirrorCS", {"start": v(126, 53) * mm, "end": v(116, 53) * mm});
            skLineSegment(sketch, "E230.MirrorCS", {"start": v(66, 53) * mm, "end": v(56, 53) * mm});
            skLineSegment(sketch, "E231.MirrorCS", {"start": v(81, 98) * mm, "end": v(71, 98) * mm});
            skLineSegment(sketch, "E232.MirrorCS", {"start": v(81, 38) * mm, "end": v(71, 38) * mm});
            skLineSegment(sketch, "E233.MirrorCS", {"start": v(96, 83) * mm, "end": v(86, 83) * mm});
            skLineSegment(sketch, "E234.MirrorCS", {"start": v(156, 113) * mm, "end": v(156, 123) * mm});
            skLineSegment(sketch, "E235.MirrorCS", {"start": v(51, 8) * mm, "end": v(41, 8) * mm});
            skLineSegment(sketch, "E236.MirrorCS", {"start": v(141, 108) * mm, "end": v(131, 108) * mm});
            skLineSegment(sketch, "E237.MirrorCS", {"start": v(141, 48) * mm, "end": v(131, 48) * mm});
            skLineSegment(sketch, "E238.MirrorCS", {"start": v(156, 93) * mm, "end": v(146, 93) * mm});
            skLineSegment(sketch, "E239.MirrorCS", {"start": v(96, 33) * mm, "end": v(86, 33) * mm});
            skLineSegment(sketch, "E240.MirrorCS", {"start": v(111, 78) * mm, "end": v(101, 78) * mm});
            skLineSegment(sketch, "E241.MirrorCS", {"start": v(111, 18) * mm, "end": v(101, 18) * mm});
            skLineSegment(sketch, "E242.MirrorCS", {"start": v(126, 63) * mm, "end": v(116, 63) * mm});
            skLineSegment(sketch, "E243.MirrorCS", {"start": v(66, 63) * mm, "end": v(56, 63) * mm});
            skLineSegment(sketch, "E244.MirrorCS", {"start": v(81, 108) * mm, "end": v(71, 108) * mm});
            skLineSegment(sketch, "E245.MirrorCS", {"start": v(81, 48) * mm, "end": v(71, 48) * mm});
            skLineSegment(sketch, "E246.MirrorCS", {"start": v(96, 93) * mm, "end": v(86, 93) * mm});
            skLineSegment(sketch, "E247.MirrorCS", {"start": v(86, 113) * mm, "end": v(86, 123) * mm});
            skLineSegment(sketch, "E248.MirrorCS", {"start": v(51, 78) * mm, "end": v(41, 78) * mm});
            skLineSegment(sketch, "E249.MirrorCS", {"start": v(146, 113) * mm, "end": v(146, 123) * mm});
            skLineSegment(sketch, "E250.MirrorCS", {"start": v(51, 18) * mm, "end": v(41, 18) * mm});
            skLineSegment(sketch, "E251.MirrorCS", {"start": v(141, 98) * mm, "end": v(141, 108) * mm});
            skLineSegment(sketch, "E252.MirrorCS", {"start": v(141, 38) * mm, "end": v(141, 48) * mm});
            skLineSegment(sketch, "E253.MirrorCS", {"start": v(156, 83) * mm, "end": v(156, 93) * mm});
            skLineSegment(sketch, "E254.MirrorCS", {"start": v(96, 23) * mm, "end": v(96, 33) * mm});
            skLineSegment(sketch, "E255.MirrorCS", {"start": v(111, 68) * mm, "end": v(111, 78) * mm});
            skLineSegment(sketch, "E256.MirrorCS", {"start": v(111, 8) * mm, "end": v(111, 18) * mm});
            skLineSegment(sketch, "E257.MirrorCS", {"start": v(126, 53) * mm, "end": v(126, 63) * mm});
            skLineSegment(sketch, "E258.MirrorCS", {"start": v(66, 53) * mm, "end": v(66, 63) * mm});
            skLineSegment(sketch, "E259.MirrorCS", {"start": v(81, 98) * mm, "end": v(81, 108) * mm});
            skLineSegment(sketch, "E260.MirrorCS", {"start": v(81, 38) * mm, "end": v(81, 48) * mm});
            skLineSegment(sketch, "E261.MirrorCS", {"start": v(96, 83) * mm, "end": v(96, 93) * mm});
            skLineSegment(sketch, "E262.MirrorCS", {"start": v(81, 113) * mm, "end": v(71, 113) * mm});
            skLineSegment(sketch, "E263.MirrorCS", {"start": v(141, 113) * mm, "end": v(131, 113) * mm});
            skLineSegment(sketch, "E264.MirrorCS", {"start": v(51, 68) * mm, "end": v(51, 78) * mm});
            skLineSegment(sketch, "E265.MirrorCS", {"start": v(51, 8) * mm, "end": v(51, 18) * mm});
            skLineSegment(sketch, "E266.MirrorCS", {"start": v(131, 98) * mm, "end": v(131, 108) * mm});
            skSolve(sketch);
        }
        {
            var Q0;
            Q0=qSketchRegion(id+"F0",true);
            var Q1;
            Q1=makeQuery(id+"F0.imprint","IMPRINT",FACE,{"disambiguationData":[TD([[makeQuery(id+"F0.imprint","IMPRINT",EDGE,{"derivedFrom":sQuery(id+"F0.wireOp",EDGE,"E4.0.0.7")}),1.0]])]});
            var Q2;
            Q2=makeQuery(id+"F0.imprint","IMPRINT",FACE,{"disambiguationData":[TD([[makeQuery(id+"F0.imprint","IMPRINT",EDGE,{"derivedFrom":sQuery(id+"F0.wireOp",EDGE,"E4.0.1.7")}),1.0]])]});
            var Q3;
            {var subQ1=sQuery(id+"F0.wireOp",EDGE,"E4.3.2.7");Q3=makeQuery(id+"F0.imprint","IMPRINT",FACE,{"disambiguationData":[TD([[makeQuery(id+"F0.imprint","IMPRINT",EDGE,{"derivedFrom":subQ1}),-1.0]])]});}
            var Q4;
            {var subQ5=sQuery(id+"F0.wireOp",EDGE,"E4.3.3.7");Q4=makeQuery(id+"F0.imprint","IMPRINT",FACE,{"disambiguationData":[TD([[makeQuery(id+"F0.imprint","IMPRINT",EDGE,{"derivedFrom":subQ5}),-1.0]])]});}
            var Q5;
            {var subQ5=sQuery(id+"F0.wireOp",EDGE,"E4.3.4.7");Q5=makeQuery(id+"F0.imprint","IMPRINT",FACE,{"disambiguationData":[TD([[makeQuery(id+"F0.imprint","IMPRINT",EDGE,{"derivedFrom":subQ5}),-1.0]])]});}
            var Q6;
            {var subQ1=sQuery(id+"F0.wireOp",EDGE,"E4.3.5.7");Q6=makeQuery(id+"F0.imprint","IMPRINT",FACE,{"disambiguationData":[TD([[makeQuery(id+"F0.imprint","IMPRINT",EDGE,{"derivedFrom":subQ1}),-1.0]])]});}
            var Q7;
            Q7=makeQuery(id+"F0.imprint","IMPRINT",FACE,{"disambiguationData":[TD([[makeQuery(id+"F0.imprint","IMPRINT",EDGE,{"derivedFrom":sQuery(id+"F0.wireOp",EDGE,"E4.0.6.7")}),1.0]])]});
            var Q8;
            Q8=makeQuery(id+"F0.imprint","IMPRINT",FACE,{"disambiguationData":[TD([[makeQuery(id+"F0.imprint","IMPRINT",EDGE,{"derivedFrom":sQuery(id+"F0.wireOp",EDGE,"E4.0.7.7")}),1.0]])]});
            var Q9;
            Q9=makeQuery(id+"F0.imprint","IMPRINT",FACE,{"disambiguationData":[TD([[makeQuery(id+"F0.imprint","IMPRINT",EDGE,{"derivedFrom":sQuery(id+"F0.wireOp",EDGE,"E3.7.6.0")}),1.0]])]});
            var Q10;
            {var subQ1=sQuery(id+"F0.wireOp",EDGE,"E3.6.6.1");Q10=makeQuery(id+"F0.imprint","IMPRINT",FACE,{"disambiguationData":[TD([[makeQuery(id+"F0.imprint","IMPRINT",EDGE,{"derivedFrom":subQ1}),-1.0]])]});}
            var Q11;
            {var subQ0=sQuery(id+"F0.wireOp",EDGE,"E3.1.6.1");var subQ1=sQuery(id+"F0.wireOp",EDGE,"E1");var subQ2=makeQuery(id+"F0.imprint","INTERSECT",VERTEX,{"derivedFrom":[subQ1,subQ0]});Q11=makeQuery(id+"F0.imprint","IMPRINT",FACE,{"disambiguationData":[TD([[makeQuery(id+"F0.imprint","IMPRINT",EDGE,{"disambiguationData":[TD([[subQ2,-1.0]])],"derivedFrom":subQ1}),-1.0]])]});}
            var Q12;
            Q12=makeQuery(id+"F0.imprint","IMPRINT",FACE,{"disambiguationData":[TD([[makeQuery(id+"F0.imprint","IMPRINT",EDGE,{"derivedFrom":sQuery(id+"F0.wireOp",EDGE,"E3.0.6.0")}),1.0]])]});
            var Q13;
            {var subQ5=sQuery(id+"F0.wireOp",EDGE,"E3.0.5.2");Q13=makeQuery(id+"F0.imprint","IMPRINT",FACE,{"disambiguationData":[TD([[makeQuery(id+"F0.imprint","IMPRINT",EDGE,{"derivedFrom":subQ5}),-1.0]])]});}
            var Q14;
            {var subQ1=sQuery(id+"F0.wireOp",EDGE,"E3.7.5.1");Q14=makeQuery(id+"F0.imprint","IMPRINT",FACE,{"disambiguationData":[TD([[makeQuery(id+"F0.imprint","IMPRINT",EDGE,{"derivedFrom":subQ1}),-1.0]])]});}
            var Q15;
            {var subQ5=sQuery(id+"F0.wireOp",EDGE,"E3.7.4.3");Q15=makeQuery(id+"F0.imprint","IMPRINT",FACE,{"disambiguationData":[TD([[makeQuery(id+"F0.imprint","IMPRINT",EDGE,{"derivedFrom":subQ5}),1.0]])]});}
            var Q16;
            {var subQ5=sQuery(id+"F0.wireOp",EDGE,"E3.7.3.3");Q16=makeQuery(id+"F0.imprint","IMPRINT",FACE,{"disambiguationData":[TD([[makeQuery(id+"F0.imprint","IMPRINT",EDGE,{"derivedFrom":subQ5}),1.0]])]});}
            var Q17;
            {var subQ1=sQuery(id+"F0.wireOp",EDGE,"E3.7.2.0");Q17=makeQuery(id+"F0.imprint","IMPRINT",FACE,{"disambiguationData":[TD([[makeQuery(id+"F0.imprint","IMPRINT",EDGE,{"derivedFrom":subQ1}),1.0]])]});}
            var Q18;
            Q18=makeQuery(id+"F0.imprint","IMPRINT",FACE,{"disambiguationData":[TD([[makeQuery(id+"F0.imprint","IMPRINT",EDGE,{"derivedFrom":sQuery(id+"F0.wireOp",EDGE,"E3.7.1.0")}),1.0]])]});
            var Q19;
            Q19=makeQuery(id+"F0.imprint","IMPRINT",FACE,{"disambiguationData":[TD([[makeQuery(id+"F0.imprint","IMPRINT",EDGE,{"derivedFrom":sQuery(id+"F0.wireOp",EDGE,"E3.7.0.0")}),1.0]])]});
            var Q20;
            Q20=makeQuery(id+"F0.imprint","IMPRINT",FACE,{"disambiguationData":[TD([[makeQuery(id+"F0.imprint","IMPRINT",EDGE,{"derivedFrom":sQuery(id+"F0.wireOp",EDGE,"E3.6.0.0")}),1.0]])]});
            var Q21;
            {var subQ0=sQuery(id+"F0.wireOp",EDGE,"E3.6.1.0");var subQ1=sQuery(id+"F0.wireOp",EDGE,"E1");var subQ2=makeQuery(id+"F0.imprint","INTERSECT",VERTEX,{"derivedFrom":[subQ1,subQ0]});Q21=makeQuery(id+"F0.imprint","IMPRINT",FACE,{"disambiguationData":[TD([[makeQuery(id+"F0.imprint","IMPRINT",EDGE,{"disambiguationData":[TD([[subQ2,-1.0]])],"derivedFrom":subQ1}),-1.0]])]});}
            var Q22;
            {var subQ5=sQuery(id+"F0.wireOp",EDGE,"E3.5.0.0");Q22=makeQuery(id+"F0.imprint","IMPRINT",FACE,{"disambiguationData":[TD([[makeQuery(id+"F0.imprint","IMPRINT",EDGE,{"derivedFrom":subQ5}),1.0]])]});}
            var Q23;
            {var subQ5=sQuery(id+"F0.wireOp",EDGE,"E3.2.0.0");Q23=makeQuery(id+"F0.imprint","IMPRINT",FACE,{"disambiguationData":[TD([[makeQuery(id+"F0.imprint","IMPRINT",EDGE,{"derivedFrom":subQ5}),1.0]])]});}
            var Q24;
            {var subQ4=sQuery(id+"F0.wireOp",EDGE,"E3.1.0.0");Q24=makeQuery(id+"F0.imprint","IMPRINT",FACE,{"disambiguationData":[TD([[makeQuery(id+"F0.imprint","IMPRINT",EDGE,{"derivedFrom":subQ4}),1.0]])]});}
            var Q25;
            Q25=makeQuery(id+"F0.imprint","IMPRINT",FACE,{"disambiguationData":[TD([[makeQuery(id+"F0.imprint","IMPRINT",EDGE,{"derivedFrom":sQuery(id+"F0.wireOp",EDGE,"E2.bottom")}),1.0]])]});
            var Q26;
            {var subQ6=sQuery(id+"F0.wireOp",EDGE,"E3.0.1.0");Q26=makeQuery(id+"F0.imprint","IMPRINT",FACE,{"disambiguationData":[TD([[makeQuery(id+"F0.imprint","IMPRINT",EDGE,{"derivedFrom":subQ6}),1.0]])]});}
            var Q27;
            {var subQ5=sQuery(id+"F0.wireOp",EDGE,"E3.0.2.2");Q27=makeQuery(id+"F0.imprint","IMPRINT",FACE,{"disambiguationData":[TD([[makeQuery(id+"F0.imprint","IMPRINT",EDGE,{"derivedFrom":subQ5}),-1.0]])]});}
            var Q28;
            {var subQ5=sQuery(id+"F0.wireOp",EDGE,"E3.0.4.2");Q28=makeQuery(id+"F0.imprint","IMPRINT",FACE,{"disambiguationData":[TD([[makeQuery(id+"F0.imprint","IMPRINT",EDGE,{"derivedFrom":subQ5}),-1.0]])]});}
            var Q29;
            {var subQ0=sQuery(id+"F0.wireOp",EDGE,"E3.1.1.2");var subQ1=sQuery(id+"F0.wireOp",EDGE,"E1");var subQ2=makeQuery(id+"F0.imprint","INTERSECT",VERTEX,{"derivedFrom":[subQ1,subQ0]});Q29=makeQuery(id+"F0.imprint","IMPRINT",FACE,{"disambiguationData":[TD([[makeQuery(id+"F0.imprint","IMPRINT",EDGE,{"disambiguationData":[TD([[subQ2,-1.0]])],"derivedFrom":subQ1}),-1.0]])]});}
            var Q30;
            {var subQ0=sQuery(id+"F0.wireOp",EDGE,"E3.3.0.0");Q30=makeQuery(id+"F0.imprint","IMPRINT",FACE,{"disambiguationData":[TD([[makeQuery(id+"F0.imprint","IMPRINT",EDGE,{"derivedFrom":subQ0}),1.0]])]});}
            var Q31;
            {var subQ5=sQuery(id+"F0.wireOp",EDGE,"E3.4.0.0");Q31=makeQuery(id+"F0.imprint","IMPRINT",FACE,{"disambiguationData":[TD([[makeQuery(id+"F0.imprint","IMPRINT",EDGE,{"derivedFrom":subQ5}),1.0]])]});}
            var Q32;
            {var subQ62=sQuery(id+"F0.wireOp",EDGE,"E3.0.2.3");Q32=makeQuery(id+"F0.imprint","IMPRINT",FACE,{"disambiguationData":[TD([[makeQuery(id+"F0.imprint","IMPRINT",EDGE,{"derivedFrom":subQ62}),-1.0]])]});}
            var Q33;
            Q33=makeQuery(id+"F0.imprint","IMPRINT",FACE,{"disambiguationData":[TD([[makeQuery(id+"F0.imprint","IMPRINT",EDGE,{"derivedFrom":sQuery(id+"F0.wireOp",EDGE,"E150.MirrorCS")}),-1.0]])]});
            var Q34;
            Q34=makeQuery(id+"F0.imprint","IMPRINT",FACE,{"disambiguationData":[TD([[makeQuery(id+"F0.imprint","IMPRINT",EDGE,{"derivedFrom":sQuery(id+"F0.wireOp",EDGE,"E87.MirrorCS")}),-1.0]])]});
            var Q35;
            {var subQ2=sQuery(id+"F0.wireOp",EDGE,"E34.MirrorCS");Q35=makeQuery(id+"F0.imprint","IMPRINT",FACE,{"disambiguationData":[TD([[makeQuery(id+"F0.imprint","IMPRINT",EDGE,{"derivedFrom":subQ2}),1.0]])]});}
            var Q36;
            {var subQ0=sQuery(id+"F0.wireOp",EDGE,"E221.MirrorCS");Q36=makeQuery(id+"F0.imprint","IMPRINT",FACE,{"disambiguationData":[TD([[makeQuery(id+"F0.imprint","IMPRINT",EDGE,{"derivedFrom":subQ0}),1.0]])]});}
            var Q37;
            {var subQ0=sQuery(id+"F0.wireOp",EDGE,"E166.MirrorCS");Q37=makeQuery(id+"F0.imprint","IMPRINT",FACE,{"disambiguationData":[TD([[makeQuery(id+"F0.imprint","IMPRINT",EDGE,{"derivedFrom":subQ0}),1.0]])]});}
            var Q38;
            {var subQ1=sQuery(id+"F0.wireOp",EDGE,"E98.MirrorCS");Q38=makeQuery(id+"F0.imprint","IMPRINT",FACE,{"disambiguationData":[TD([[makeQuery(id+"F0.imprint","IMPRINT",EDGE,{"derivedFrom":subQ1}),1.0]])]});}
            var Q39;
            Q39=makeQuery(id+"F0.imprint","IMPRINT",FACE,{"disambiguationData":[TD([[makeQuery(id+"F0.imprint","IMPRINT",EDGE,{"derivedFrom":sQuery(id+"F0.wireOp",EDGE,"E33.MirrorCS")}),1.0]])]});
            var Q40;
            Q40=makeQuery(id+"F0.imprint","IMPRINT",FACE,{"disambiguationData":[TD([[makeQuery(id+"F0.imprint","IMPRINT",EDGE,{"derivedFrom":sQuery(id+"F0.wireOp",EDGE,"E207.MirrorCS")}),-1.0]])]});
            var Q41;
            {var subQ0=sQuery(id+"F0.wireOp",EDGE,"E236.MirrorCS");var subQ1=sQuery(id+"F0.wireOp",EDGE,"E25.MirrorC");var subQ2=makeQuery(id+"F0.imprint","INTERSECT",VERTEX,{"derivedFrom":[subQ1,subQ0]});Q41=makeQuery(id+"F0.imprint","IMPRINT",FACE,{"disambiguationData":[TD([[makeQuery(id+"F0.imprint","IMPRINT",EDGE,{"disambiguationData":[TD([[subQ2,-1.0]])],"derivedFrom":subQ1}),1.0]])]});}
            var Q42;
            Q42=makeQuery(id+"F0.imprint","IMPRINT",FACE,{"disambiguationData":[TD([[makeQuery(id+"F0.imprint","IMPRINT",EDGE,{"derivedFrom":sQuery(id+"F0.wireOp",EDGE,"E48.MirrorCS")}),-1.0]])]});
            var Q43;
            {var subQ5=sQuery(id+"F0.wireOp",EDGE,"E253.MirrorCS");Q43=makeQuery(id+"F0.imprint","IMPRINT",FACE,{"disambiguationData":[TD([[makeQuery(id+"F0.imprint","IMPRINT",EDGE,{"derivedFrom":subQ5}),1.0]])]});}
            var Q44;
            {var subQ0=sQuery(id+"F0.wireOp",EDGE,"E191.MirrorCS");Q44=makeQuery(id+"F0.imprint","IMPRINT",FACE,{"disambiguationData":[TD([[makeQuery(id+"F0.imprint","IMPRINT",EDGE,{"derivedFrom":subQ0}),1.0]])]});}
            var Q45;
            Q45=makeQuery(id+"F0.imprint","IMPRINT",FACE,{"disambiguationData":[TD([[makeQuery(id+"F0.imprint","IMPRINT",EDGE,{"derivedFrom":sQuery(id+"F0.wireOp",EDGE,"E112.MirrorCS")}),-1.0]])]});
            var Q46;
            {var subQ1=sQuery(id+"F0.wireOp",EDGE,"E73.MirrorCS");Q46=makeQuery(id+"F0.imprint","IMPRINT",FACE,{"disambiguationData":[TD([[makeQuery(id+"F0.imprint","IMPRINT",EDGE,{"derivedFrom":subQ1}),1.0]])]});}
            var Q47;
            {var subQ0=sQuery(id+"F0.wireOp",EDGE,"E32.MirrorCS");Q47=makeQuery(id+"F0.imprint","IMPRINT",FACE,{"disambiguationData":[TD([[makeQuery(id+"F0.imprint","IMPRINT",EDGE,{"derivedFrom":subQ0}),-1.0]])]});}
            var Q48;
            {var subQ0=sQuery(id+"F0.wireOp",EDGE,"E223.MirrorCS");Q48=makeQuery(id+"F0.imprint","IMPRINT",FACE,{"disambiguationData":[TD([[makeQuery(id+"F0.imprint","IMPRINT",EDGE,{"derivedFrom":subQ0}),-1.0]])]});}
            var Q49;
            {var subQ5=sQuery(id+"F0.wireOp",EDGE,"E106.MirrorCS");Q49=makeQuery(id+"F0.imprint","IMPRINT",FACE,{"disambiguationData":[TD([[makeQuery(id+"F0.imprint","IMPRINT",EDGE,{"derivedFrom":subQ5}),-1.0]])]});}
            var Q50;
            Q50=makeQuery(id+"F0.imprint","IMPRINT",FACE,{"disambiguationData":[TD([[makeQuery(id+"F0.imprint","IMPRINT",EDGE,{"derivedFrom":sQuery(id+"F0.wireOp",EDGE,"E53.MirrorCS")}),-1.0]])]});
            var Q51;
            Q51=makeQuery(id+"F0.imprint","IMPRINT",FACE,{"disambiguationData":[TD([[makeQuery(id+"F0.imprint","IMPRINT",EDGE,{"derivedFrom":sQuery(id+"F0.wireOp",EDGE,"E31.MirrorCS")}),-1.0]])]});
            var Q52;
            Q52=makeQuery(id+"F0.imprint","IMPRINT",FACE,{"disambiguationData":[TD([[makeQuery(id+"F0.imprint","IMPRINT",EDGE,{"derivedFrom":sQuery(id+"F0.wireOp",EDGE,"E55.MirrorCS")}),-1.0]])]});
            var Q53;
            {var subQ0=sQuery(id+"F0.wireOp",EDGE,"E108.MirrorCS");var subQ1=sQuery(id+"F0.wireOp",EDGE,"E25.MirrorC");var subQ2=makeQuery(id+"F0.imprint","INTERSECT",VERTEX,{"derivedFrom":[subQ1,subQ0]});Q53=makeQuery(id+"F0.imprint","IMPRINT",FACE,{"disambiguationData":[TD([[makeQuery(id+"F0.imprint","IMPRINT",EDGE,{"disambiguationData":[TD([[subQ2,-1.0]])],"derivedFrom":subQ1}),1.0]])]});}
            var Q54;
            {var subQ5=sQuery(id+"F0.wireOp",EDGE,"E118.MirrorCS");Q54=makeQuery(id+"F0.imprint","IMPRINT",FACE,{"disambiguationData":[TD([[makeQuery(id+"F0.imprint","IMPRINT",EDGE,{"derivedFrom":subQ5}),-1.0]])]});}
            var Q55;
            {var subQ0=sQuery(id+"F0.wireOp",EDGE,"E46.MirrorCS");Q55=makeQuery(id+"F0.imprint","IMPRINT",FACE,{"disambiguationData":[TD([[makeQuery(id+"F0.imprint","IMPRINT",EDGE,{"derivedFrom":subQ0}),-1.0]])]});}
            var Q56;
            {var subQ1=sQuery(id+"F0.wireOp",EDGE,"E117.MirrorCS");Q56=makeQuery(id+"F0.imprint","IMPRINT",FACE,{"disambiguationData":[TD([[makeQuery(id+"F0.imprint","IMPRINT",EDGE,{"derivedFrom":subQ1}),-1.0]])]});}
            var Q57;
            Q57=makeQuery(id+"F0.imprint","IMPRINT",FACE,{"disambiguationData":[TD([[makeQuery(id+"F0.imprint","IMPRINT",EDGE,{"derivedFrom":sQuery(id+"F0.wireOp",EDGE,"E21.MirrorCS")}),-1.0]])]});
            var Q58;
            {var subQ1=sQuery(id+"F0.wireOp",EDGE,"E6.MirrorCS");Q58=makeQuery(id+"F0.imprint","IMPRINT",FACE,{"disambiguationData":[TD([[makeQuery(id+"F0.imprint","IMPRINT",EDGE,{"derivedFrom":subQ1}),1.0]])]});}
            var Q59;
            {var subQ0=sQuery(id+"F0.wireOp",EDGE,"E29.MirrorCS");Q59=makeQuery(id+"F0.imprint","IMPRINT",FACE,{"disambiguationData":[TD([[makeQuery(id+"F0.imprint","IMPRINT",EDGE,{"derivedFrom":subQ0}),1.0]])]});}
            var Q60;
            {var subQ0=sQuery(id+"F0.wireOp",EDGE,"E17.MirrorCS");Q60=makeQuery(id+"F0.imprint","IMPRINT",FACE,{"disambiguationData":[TD([[makeQuery(id+"F0.imprint","IMPRINT",EDGE,{"derivedFrom":subQ0}),-1.0]])]});}
            var Q61;
            Q61=makeQuery(id+"F0.imprint","IMPRINT",FACE,{"disambiguationData":[TD([[makeQuery(id+"F0.imprint","IMPRINT",EDGE,{"derivedFrom":sQuery(id+"F0.wireOp",EDGE,"E35.MirrorCS")}),1.0]])]});
            var Q62;
            {var subQ0=sQuery(id+"F0.wireOp",EDGE,"E9.MirrorCS");Q62=makeQuery(id+"F0.imprint","IMPRINT",FACE,{"disambiguationData":[TD([[makeQuery(id+"F0.imprint","IMPRINT",EDGE,{"derivedFrom":subQ0}),1.0]])]});}
            var Q63;
            {var subQ0=sQuery(id+"F0.wireOp",EDGE,"E196.MirrorCS");var subQ1=sQuery(id+"F0.wireOp",EDGE,"E25.MirrorC");var subQ2=makeQuery(id+"F0.imprint","INTERSECT",VERTEX,{"derivedFrom":[subQ1,subQ0]});Q63=makeQuery(id+"F0.imprint","IMPRINT",FACE,{"disambiguationData":[TD([[makeQuery(id+"F0.imprint","IMPRINT",EDGE,{"disambiguationData":[TD([[subQ2,-1.0]])],"derivedFrom":subQ1}),1.0]])]});}
            var Q64;
            {var subQ5=sQuery(id+"F0.wireOp",EDGE,"E10.MirrorCS");Q64=makeQuery(id+"F0.imprint","IMPRINT",FACE,{"disambiguationData":[TD([[makeQuery(id+"F0.imprint","IMPRINT",EDGE,{"derivedFrom":subQ5}),-1.0]])]});}
            var Q65;
            {var subQ0=sQuery(id+"F0.wireOp",EDGE,"E197.MirrorCS");Q65=makeQuery(id+"F0.imprint","IMPRINT",FACE,{"disambiguationData":[TD([[makeQuery(id+"F0.imprint","IMPRINT",EDGE,{"derivedFrom":subQ0}),1.0]])]});}
            extrude(context, id + "F1", {"entities" : qUnion([Q0, Q1, Q2, Q3, Q4, Q5, Q6, Q7, Q8, Q9, Q10, Q11, Q12, Q13, Q14, Q15, Q16, Q17, Q18, Q19, Q20, Q21, Q22, Q23, Q24, Q25, Q26, Q27, Q28, Q29, Q30, Q31, Q32, Q33, Q34, Q35, Q36, Q37, Q38, Q39, Q40, Q41, Q42, Q43, Q44, Q45, Q46, Q47, Q48, Q49, Q50, Q51, Q52, Q53, Q54, Q55, Q56, Q57, Q58, Q59, Q60, Q61, Q62, Q63, Q64, Q65]), "depth" : 25 * mm});
        }
    });
